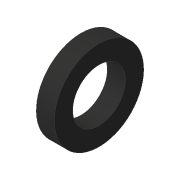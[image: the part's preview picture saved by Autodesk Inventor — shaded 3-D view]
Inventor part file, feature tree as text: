
AUTODESK INVENTOR PART (.ipt)
format: ipt  version: 2018 (Build 220112000, 112)  size: 83,456 bytes
history: native  units: in
note: dims shown in document units (in); Inventor stores cm internally (conversion verified against a paired STEP export)
features: plane x2, extrude x1, sketch x1
ambient origin geometry x8: Origin, YZ Plane, XZ Plane, XY Plane, X Axis, Y Axis, Z Axis, Center Point
bodies: Solid1 (feature_tree)
feature tree (4):
  extrude  "Extrusion1"  Depth=5.5in
  plane  "Work Plane2"
  sketch  "Sketch1"  dims[d0=16.0in d1=27.13in d2=5.5in d3=0.0in]
  plane  "Work Plane1"
